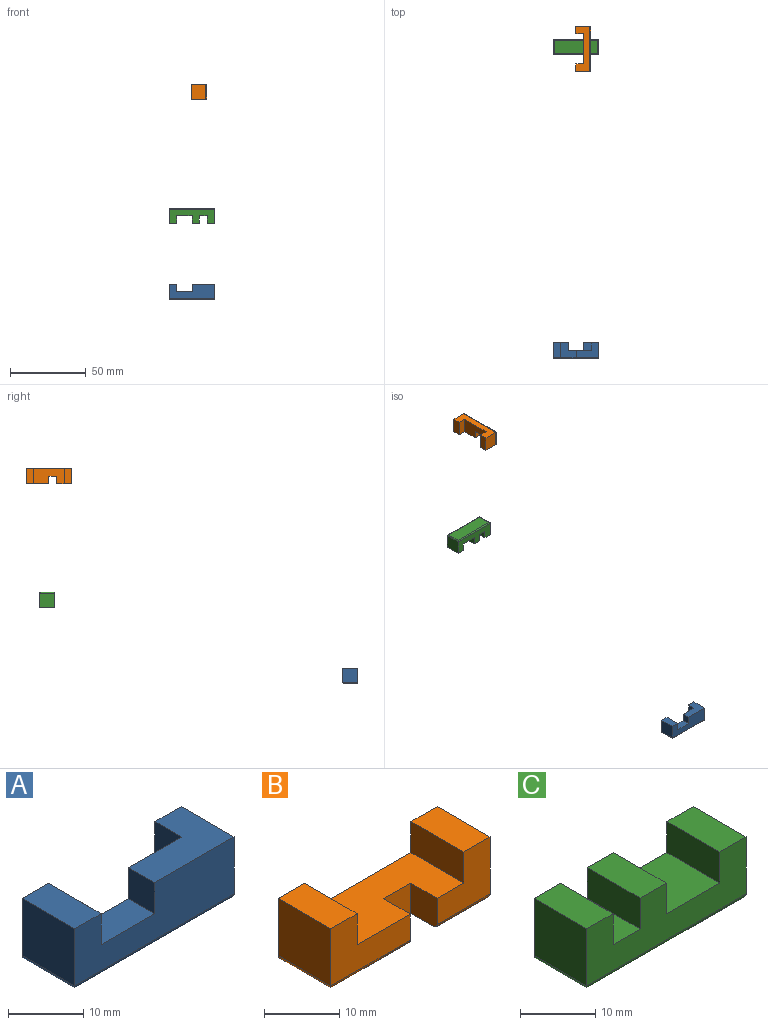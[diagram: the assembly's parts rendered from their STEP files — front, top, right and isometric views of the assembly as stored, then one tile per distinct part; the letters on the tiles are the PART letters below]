
ASSEMBLY  parts=3 mates=3
PART A: 21 faces, bbox 30x10x10 mm
  f0: plane 9.95x9.33mm, normal (0,1,0), area 67.5mm2, adj f6,f7,f9,f13,f14,f20
  f1: plane 5.05x5mm, normal (0,0,1), area 25.2mm2, adj f5,f11,f12,f15
  f2: plane 30x9.33mm, normal (0,-1,0), area 228.7mm2, adj f3,f4,f6,f7,f9,f10,f13,f18
  f3: plane 14.95x9.95mm, normal (0,0,1), area 98.3mm2, adj f2,f4,f5,f10,f11,f12
  f4: plane 9.95x9.33mm, normal (1,0,0), area 92.8mm2, adj f2,f3,f5,f17
  f5: plane 9.95x9.33mm, normal (0,1,0), area 67.5mm2, adj f1,f3,f4,f12,f15,f16
  f6: plane 9.95x9.33mm, normal (-1,0,0), area 92.8mm2, adj f0,f2,f7,f19
  f7: plane 9.95x4.95mm, normal (0,0,1), area 49.3mm2, adj f0,f2,f6,f9
  f8: plane 28.75x8.7mm, normal (0,0,-1), area 205.4mm2, adj f11,f14,f15,f16,f17,f18,f19,f20
  f9: plane 9.95x5.05mm, normal (1,0,0), area 50.2mm2, adj f0,f2,f7,f13
  f10: plane 5.05x4.9mm, normal (-1,0,0), area 24.7mm2, adj f2,f3,f11,f13
  f11: plane 15.1x9.95mm, normal (0,1,0), area 100mm2, adj f1,f3,f8,f10,f12,f13,f14,f15
  f12: plane 5.05x5.05mm, normal (-1,0,0), area 25.5mm2, adj f1,f3,f5,f11
  f13: plane 10.1x9.95mm, normal (0,0,1), area 74.7mm2, adj f0,f2,f9,f10,f11,f14
  f14: plane 5.05x4.9mm, normal (1,0,0), area 24.7mm2, adj f0,f8,f11,f13,f20
  f15: plane 5.05x4.9mm, normal (-1,0,0), area 24.7mm2, adj f1,f5,f8,f11,f16
  f16: cylinder r=0.62mm len=9.95mm, axis (-1,0,0), area 9.5mm2, adj f5,f8,f15,f17
  f17: cylinder r=0.62mm len=9.95mm, axis (0,1,0), area 9.3mm2, adj f4,f8,f16,f18
  f18: cylinder r=0.62mm len=30mm, axis (1,0,0), area 29mm2, adj f2,f8,f17,f19
  f19: cylinder r=0.62mm len=9.95mm, axis (0,-1,0), area 9.3mm2, adj f6,f8,f18,f20
  f20: cylinder r=0.62mm len=9.95mm, axis (-1,0,0), area 9.5mm2, adj f0,f8,f14,f19
PART B: 19 faces, bbox 30x10x10 mm
  f0: plane 14.95x9.33mm, normal (0,-1,0), area 88.9mm2, adj f5,f6,f8,f10,f11,f18
  f1: plane 9.95x4.95mm, normal (0,0,1), area 49.3mm2, adj f2,f3,f4,f9
  f2: plane 9.95x9.33mm, normal (0,-1,0), area 67.5mm2, adj f1,f3,f9,f10,f12,f14
  f3: plane 9.95x9.33mm, normal (1,0,0), area 92.8mm2, adj f1,f2,f4,f15
  f4: plane 30x9.33mm, normal (0,1,0), area 178.2mm2, adj f1,f3,f5,f6,f8,f9,f10,f16
  f5: plane 9.95x9.33mm, normal (-1,0,0), area 92.8mm2, adj f0,f4,f6,f17
  f6: plane 9.95x4.95mm, normal (0,0,1), area 49.3mm2, adj f0,f4,f5,f8
  f7: plane 28.75x8.7mm, normal (0,0,-1), area 227.9mm2, adj f11,f12,f13,f14,f15,f16,f17,f18
  f8: plane 9.95x5.05mm, normal (1,0,0), area 50.2mm2, adj f0,f4,f6,f10
  f9: plane 9.95x5.05mm, normal (-1,0,0), area 50.2mm2, adj f1,f2,f4,f10
  f10: plane 20.1x9.95mm, normal (0,0,1), area 174.6mm2, adj f0,f2,f4,f8,f9,f11,f12,f13
  f11: plane 4.98x4.9mm, normal (1,0,0), area 24.3mm2, adj f0,f7,f10,f13,f18
  f12: plane 4.98x4.9mm, normal (-1,0,0), area 24.3mm2, adj f2,f7,f10,f13,f14
  f13: plane 5.1x4.9mm, normal (0,-1,0), area 25mm2, adj f7,f10,f11,f12
  f14: cylinder r=0.62mm len=9.95mm, axis (1,0,0), area 9.5mm2, adj f2,f7,f12,f15
  f15: cylinder r=0.62mm len=9.95mm, axis (0,1,0), area 9.3mm2, adj f3,f7,f14,f16
  f16: cylinder r=0.62mm len=30mm, axis (-1,0,0), area 29mm2, adj f4,f7,f15,f17
  f17: cylinder r=0.62mm len=9.95mm, axis (0,-1,0), area 9.3mm2, adj f5,f7,f16,f18
  f18: cylinder r=0.62mm len=14.95mm, axis (1,0,0), area 14.5mm2, adj f0,f7,f11,f17
PART C: 18 faces, bbox 30x10x10 mm
  f0: plane 9.95x4.95mm, normal (0,0,1), area 49.3mm2, adj f2,f3,f4,f12
  f1: plane 9.95x4.9mm, normal (0,0,1), area 48.8mm2, adj f2,f4,f9,f11
  f2: plane 30x9.33mm, normal (0,-1,0), area 203mm2, adj f0,f1,f3,f5,f6,f8,f9,f10
  f3: plane 9.95x9.33mm, normal (1,0,0), area 92.8mm2, adj f0,f2,f4,f15
  f4: plane 30x9.33mm, normal (0,1,0), area 203mm2, adj f0,f1,f3,f5,f6,f8,f9,f10
  f5: plane 9.95x9.33mm, normal (-1,0,0), area 92.8mm2, adj f2,f4,f6,f16
  f6: plane 9.95x4.95mm, normal (0,0,1), area 49.3mm2, adj f2,f4,f5,f8
  f7: plane 28.75x8.7mm, normal (0,0,-1), area 250.1mm2, adj f14,f15,f16,f17
  f8: plane 9.95x5.05mm, normal (1,0,0), area 50.2mm2, adj f2,f4,f6,f10
  f9: plane 9.95x5.05mm, normal (-1,0,0), area 50.2mm2, adj f1,f2,f4,f10
  f10: plane 9.95x5.1mm, normal (0,0,1), area 50.7mm2, adj f2,f4,f8,f9
  f11: plane 9.95x5.05mm, normal (1,0,0), area 50.2mm2, adj f1,f2,f4,f13
  f12: plane 9.95x5.05mm, normal (-1,0,0), area 50.2mm2, adj f0,f2,f4,f13
  f13: plane 10.1x9.95mm, normal (0,0,1), area 100.5mm2, adj f2,f4,f11,f12
  f14: cylinder r=0.62mm len=30mm, axis (1,0,0), area 29mm2, adj f2,f7,f15,f16
  f15: cylinder r=0.62mm len=9.95mm, axis (0,1,0), area 9.3mm2, adj f3,f7,f14,f17
  f16: cylinder r=0.62mm len=9.95mm, axis (0,-1,0), area 9.3mm2, adj f5,f7,f14,f17
  f17: cylinder r=0.62mm len=30mm, axis (-1,0,0), area 29mm2, adj f4,f7,f15,f16
PLACE A t=(-12.78,-286,68.61)mm
PLACE B rot(axis=(0.58,-0.58,-0.58),120deg) t=(-2.93,12.93,255.04)mm
PLACE C rot(axis=(0,1,0),180deg) t=(-12.78,14,128.61)mm
MATE parallel B.f13 <-> A.f3  axis (0,0,-1) through (-5.38,10.43,205.04)mm
MATE parallel C.f0 <-> A.f7  axis (0,0,-1) through (-25.31,14,118.66)mm
MATE planar B.f10 <-> C.f9  axis (-1,0,0) through (-7.83,13.29,205.4)mm
